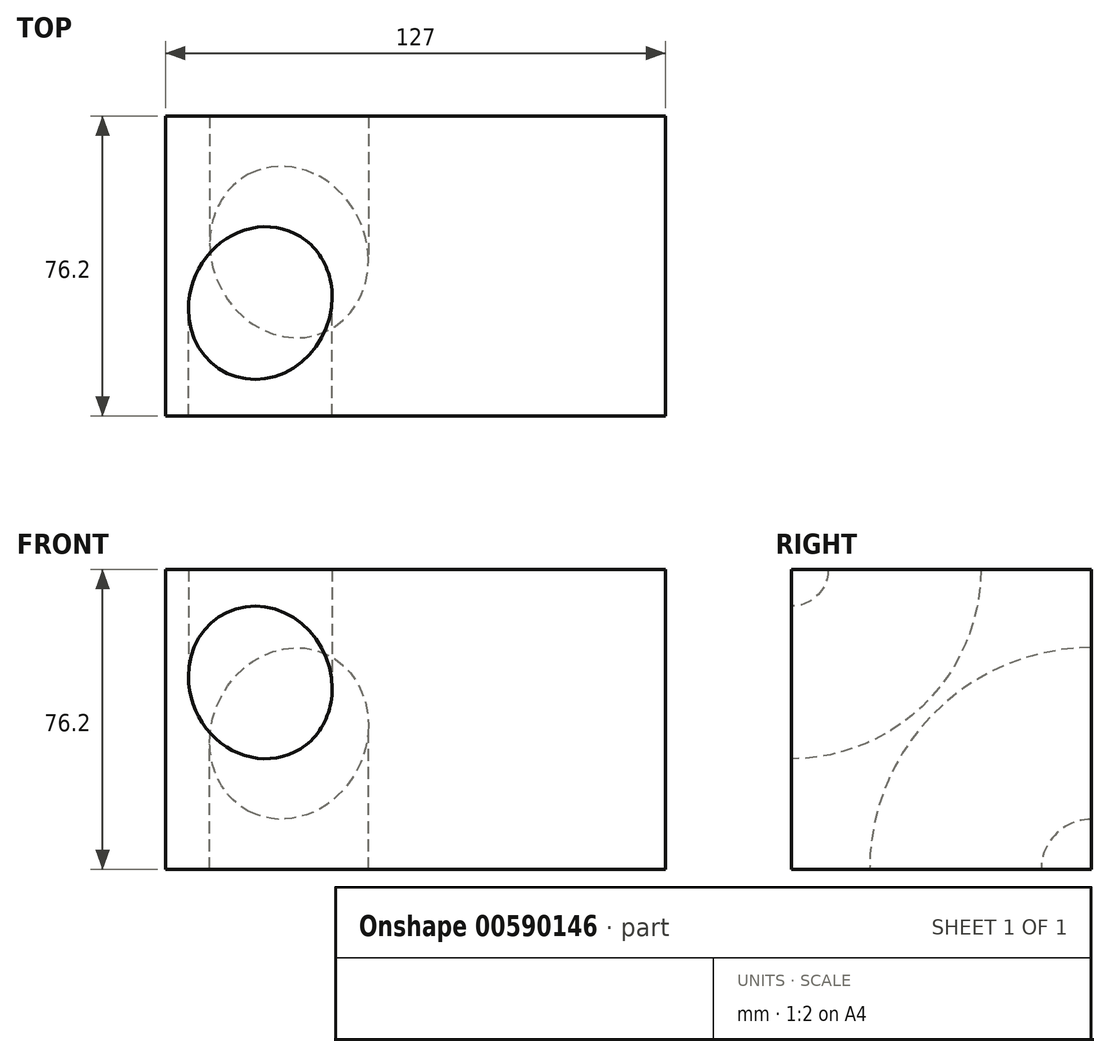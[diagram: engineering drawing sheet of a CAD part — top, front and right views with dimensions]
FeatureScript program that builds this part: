
annotation { "Feature Type Name" : "Feature", "Feature Type Description" : "" }
export const myFeature = defineFeature(function(context is Context, id is Id, definition is map)
    precondition{}
    {
        {
            var Q0;
            Q0=qCreatedBy(makeId("Front.planeOp"),FACE);
            var sketch = newSketch(context, id + "F0", { "sketchPlane" : qUnion([Q0])});
            skLineSegment(sketch, "E0.bottom", {"start": v(0, 0) * mm, "end": v(127, 0) * mm});
            skLineSegment(sketch, "E0.top", {"start": v(0, 76.2) * mm, "end": v(127, 76.2) * mm});
            skLineSegment(sketch, "E0.left", {"start": v(0, 0) * mm, "end": v(0, 76.2) * mm});
            skLineSegment(sketch, "E0.right", {"start": v(127, 0) * mm, "end": v(127, 76.2) * mm});
            skSolve(sketch);
        }
        {
            var Q0;
            Q0=makeQuery(id+"F0.imprint","IMPRINT",FACE,{"disambiguationData":[TD([[makeQuery(id+"F0.imprint","IMPRINT",EDGE,{"derivedFrom":sQuery(id+"F0.wireOp",EDGE,"E0.bottom")}),1.0]])]});
            extrude(context, id + "F1", {"entities" : qUnion([Q0]), "depth" : 76.2 * mm, "offsetDistance" : 25.4 * mm});
        }
        {
            var Q0;
            Q0=makeQuery(id+"F1.opExtrude","CAP_FACE",FACE,{"disambiguationData":[OSD([sQuery(id+"F0.wireOp",EDGE,"E0.bottom"),sQuery(id+"F0.wireOp",EDGE,"E0.top"),sQuery(id+"F0.wireOp",EDGE,"E0.left"),sQuery(id+"F0.wireOp",EDGE,"E0.right")])],"isStart":false});
            var sketch = newSketch(context, id + "F2", { "sketchPlane" : qUnion([Q0])});
            skEllipse(sketch, "E1", {"center": v(24.06, 47.5) * mm, "majorRadius": 19.73 * mm, "minorRadius": 17.9 * mm, "majorAxis": v(0.44, -0.9)});
            skSolve(sketch);
        }
        {
            var Q0;
            Q0=makeQuery(id+"F2.imprint","IMPRINT",FACE,{"disambiguationData":[TD([[makeQuery(id+"F2.imprint","IMPRINT",EDGE,{"derivedFrom":sQuery(id+"F2.wireOp",EDGE,"E1")}),1.0]])]});
            var Q1;
            Q1=makeQuery(id+"F1.opExtrude","CAP_EDGE",EDGE,{"disambiguationData":[OSD([sQuery(id+"F0.wireOp",EDGE,"E0.top")])],"isStart":false});
            revolve(context, id + "F3", {"entities" : qUnion([Q0]), "axis" : qUnion([Q1]), "revolveType" : RevolveType.FULL});
        }
        {
            var Q0;
            Q0=makeQuery(id+"F1.opExtrude","CAP_FACE",FACE,{"disambiguationData":[OSD([sQuery(id+"F0.wireOp",EDGE,"E0.bottom"),sQuery(id+"F0.wireOp",EDGE,"E0.top"),sQuery(id+"F0.wireOp",EDGE,"E0.left"),sQuery(id+"F0.wireOp",EDGE,"E0.right")])],"isStart":true});
            var sketch = newSketch(context, id + "F4", { "sketchPlane" : qUnion([Q0])});
            skEllipse(sketch, "E2", {"center": v(-31.36, 34.54) * mm, "majorRadius": 22.27 * mm, "minorRadius": 19.61 * mm, "majorAxis": v(0.43, -0.9)});
            skSolve(sketch);
        }
        {
            var Q0;
            Q0=makeQuery(id+"F4.imprint","IMPRINT",FACE,{"disambiguationData":[TD([[makeQuery(id+"F4.imprint","IMPRINT",EDGE,{"derivedFrom":sQuery(id+"F4.wireOp",EDGE,"E2")}),1.0]])]});
            var Q1;
            Q1=makeQuery(id+"F1.opExtrude","CAP_EDGE",EDGE,{"disambiguationData":[OSD([sQuery(id+"F0.wireOp",EDGE,"E0.bottom")])],"isStart":true});
            revolve(context, id + "F5", {"entities" : qUnion([Q0]), "axis" : qUnion([Q1]), "revolveType" : RevolveType.FULL});
        }
        {
            var Q0;
            Q0=makeQuery(id+"F3.opRevolve","SWEPT_BODY",BODY,{"disambiguationData":[OSD([sQuery(id+"F2.wireOp",EDGE,"E1")])]});
            var Q1;
            Q1=makeQuery(id+"F5.opRevolve","SWEPT_BODY",BODY,{"disambiguationData":[OSD([sQuery(id+"F4.wireOp",EDGE,"E2")])]});
            var Q2;
            Q2=makeQuery(id+"F1.opExtrude","SWEPT_BODY",BODY,{"disambiguationData":[OSD([sQuery(id+"F0.wireOp",EDGE,"E0.bottom"),sQuery(id+"F0.wireOp",EDGE,"E0.top"),sQuery(id+"F0.wireOp",EDGE,"E0.left"),sQuery(id+"F0.wireOp",EDGE,"E0.right")])]});
            booleanBodies(context, id + "F6", {"operationType" : BooleanOperationType.SUBTRACTION, "tools" : qUnion([Q0, Q1]), "targets" : qUnion([Q2])});
        }
    });
